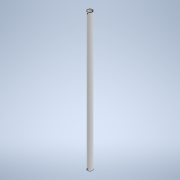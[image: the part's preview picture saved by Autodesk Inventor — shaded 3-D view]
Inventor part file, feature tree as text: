
AUTODESK INVENTOR PART (.ipt)
format: ipt  version: 2022 (Build 260153000, 153)  size: 169,984 bytes
history: native  units: mm
features: extrude x2, sketch x2
ambient origin geometry x8: Origin, YZ Plane, XZ Plane, XY Plane, X Axis, Y Axis, Z Axis, Center Point
bodies: Body1 (feature_tree)
feature tree (4):
  extrude  "Extrusion5"  Depth=18.0mm
  extrude  "Extrusion6"  Depth=10.0mm TaperAngle=0.0deg
  sketch  "Sketch2"  dims[d31=34.456mm d91=18.0mm]
  sketch  "Sketch3"  dims[d92=16.0mm d93=500.0mm d94=0.0mm d95=5.0mm d96=3.0mm d97=5.0mm d98=3.0mm d99=10.0mm d100=10.0mm d101=0.0mm d102=0.0mm]
